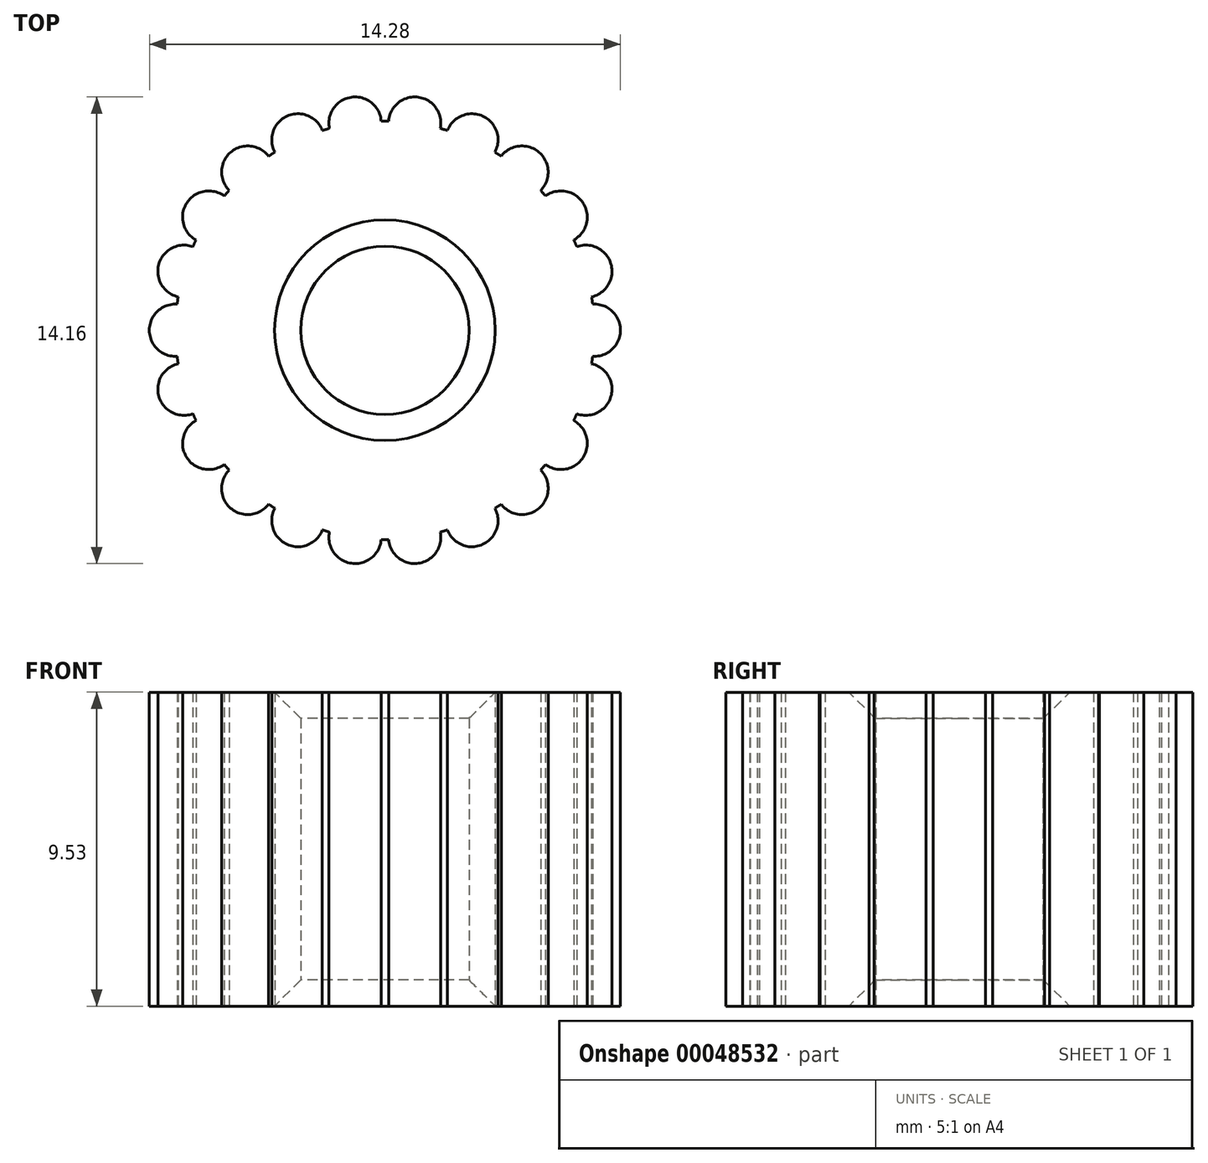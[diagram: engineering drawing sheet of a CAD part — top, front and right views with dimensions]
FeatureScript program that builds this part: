
annotation { "Feature Type Name" : "Feature", "Feature Type Description" : "" }
export const myFeature = defineFeature(function(context is Context, id is Id, definition is map)
    precondition{}
    {
        {
            var Q0;
            Q0=qCreatedBy(makeId("Top.planeOp"),FACE);
            var sketch = newSketch(context, id + "F0", { "sketchPlane" : qUnion([Q0])});
            skCircle(sketch, "E0", {"center": v(0, 0) * mm, "radius": 2.55 * mm});
            skCircle(sketch, "E1", {"center": v(0, 0) * mm, "radius": 6.35 * mm});
            skCircle(sketch, "E2", {"center": v(-6.35, 0) * mm, "radius": 0.8 * mm});
            skCircle(sketch, "E3.1.0", {"center": v(-6.1, -1.79) * mm, "radius": 0.8 * mm});
            skCircle(sketch, "E3.2.0", {"center": v(-5.34, -3.43) * mm, "radius": 0.8 * mm});
            skCircle(sketch, "E3.3.0", {"center": v(-4.16, -4.8) * mm, "radius": 0.8 * mm});
            skCircle(sketch, "E3.4.0", {"center": v(-2.64, -5.78) * mm, "radius": 0.8 * mm});
            skCircle(sketch, "E3.5.0", {"center": v(-0.9, -6.29) * mm, "radius": 0.8 * mm});
            skCircle(sketch, "E3.6.0", {"center": v(0.9, -6.29) * mm, "radius": 0.8 * mm});
            skCircle(sketch, "E3.7.0", {"center": v(2.64, -5.78) * mm, "radius": 0.8 * mm});
            skCircle(sketch, "E3.8.0", {"center": v(4.16, -4.8) * mm, "radius": 0.8 * mm});
            skCircle(sketch, "E3.9.0", {"center": v(5.34, -3.43) * mm, "radius": 0.8 * mm});
            skCircle(sketch, "E3.10.0", {"center": v(6.1, -1.79) * mm, "radius": 0.8 * mm});
            skCircle(sketch, "E3.11.0", {"center": v(6.35, 0) * mm, "radius": 0.8 * mm});
            skCircle(sketch, "E3.12.0", {"center": v(6.1, 1.79) * mm, "radius": 0.8 * mm});
            skCircle(sketch, "E3.13.0", {"center": v(5.34, 3.43) * mm, "radius": 0.8 * mm});
            skCircle(sketch, "E3.14.0", {"center": v(4.16, 4.8) * mm, "radius": 0.8 * mm});
            skCircle(sketch, "E3.15.0", {"center": v(2.64, 5.78) * mm, "radius": 0.8 * mm});
            skCircle(sketch, "E3.16.0", {"center": v(0.9, 6.29) * mm, "radius": 0.8 * mm});
            skCircle(sketch, "E3.17.0", {"center": v(-0.9, 6.29) * mm, "radius": 0.8 * mm});
            skCircle(sketch, "E3.18.0", {"center": v(-2.64, 5.78) * mm, "radius": 0.8 * mm});
            skCircle(sketch, "E3.19.0", {"center": v(-4.16, 4.8) * mm, "radius": 0.8 * mm});
            skCircle(sketch, "E3.20.0", {"center": v(-5.34, 3.43) * mm, "radius": 0.8 * mm});
            skCircle(sketch, "E3.21.0", {"center": v(-6.1, 1.79) * mm, "radius": 0.8 * mm});
            skSolve(sketch);
        }
        {
            var Q0;
            Q0=makeQuery(id+"F0.imprint","IMPRINT",FACE,{"disambiguationData":[TD([[makeQuery(id+"F0.imprint","IMPRINT",EDGE,{"derivedFrom":sQuery(id+"F0.wireOp",EDGE,"E0")}),-1.0]])]});
            var Q1;
            {var subQ0=sQuery(id+"F0.wireOp",EDGE,"E3.19.0");var subQ1=sQuery(id+"F0.wireOp",EDGE,"E1");var subQ3=makeQuery(id+"F0.imprint","INTERSECT",VERTEX,{"disambiguationData":[OD(0.0)],"derivedFrom":[subQ1,subQ0]});Q1=makeQuery(id+"F0.imprint","IMPRINT",FACE,{"disambiguationData":[TD([[makeQuery(id+"F0.imprint","IMPRINT",EDGE,{"disambiguationData":[TD([[subQ3,-1.0]])],"derivedFrom":subQ1}),1.0]])]});}
            var Q2;
            {var subQ0=sQuery(id+"F0.wireOp",EDGE,"E3.18.0");var subQ1=sQuery(id+"F0.wireOp",EDGE,"E1");var subQ3=makeQuery(id+"F0.imprint","INTERSECT",VERTEX,{"disambiguationData":[OD(0.0)],"derivedFrom":[subQ1,subQ0]});Q2=makeQuery(id+"F0.imprint","IMPRINT",FACE,{"disambiguationData":[TD([[makeQuery(id+"F0.imprint","IMPRINT",EDGE,{"disambiguationData":[TD([[subQ3,-1.0]])],"derivedFrom":subQ1}),1.0]])]});}
            var Q3;
            {var subQ0=sQuery(id+"F0.wireOp",EDGE,"E3.17.0");var subQ1=sQuery(id+"F0.wireOp",EDGE,"E1");var subQ3=makeQuery(id+"F0.imprint","INTERSECT",VERTEX,{"disambiguationData":[OD(0.0)],"derivedFrom":[subQ1,subQ0]});Q3=makeQuery(id+"F0.imprint","IMPRINT",FACE,{"disambiguationData":[TD([[makeQuery(id+"F0.imprint","IMPRINT",EDGE,{"disambiguationData":[TD([[subQ3,-1.0]])],"derivedFrom":subQ1}),1.0]])]});}
            var Q4;
            {var subQ0=sQuery(id+"F0.wireOp",EDGE,"E3.16.0");var subQ1=sQuery(id+"F0.wireOp",EDGE,"E1");var subQ3=makeQuery(id+"F0.imprint","INTERSECT",VERTEX,{"disambiguationData":[OD(0.0)],"derivedFrom":[subQ1,subQ0]});Q4=makeQuery(id+"F0.imprint","IMPRINT",FACE,{"disambiguationData":[TD([[makeQuery(id+"F0.imprint","IMPRINT",EDGE,{"disambiguationData":[TD([[subQ3,-1.0]])],"derivedFrom":subQ1}),1.0]])]});}
            var Q5;
            {var subQ0=sQuery(id+"F0.wireOp",EDGE,"E3.15.0");var subQ1=sQuery(id+"F0.wireOp",EDGE,"E1");var subQ3=makeQuery(id+"F0.imprint","INTERSECT",VERTEX,{"disambiguationData":[OD(0.0)],"derivedFrom":[subQ1,subQ0]});Q5=makeQuery(id+"F0.imprint","IMPRINT",FACE,{"disambiguationData":[TD([[makeQuery(id+"F0.imprint","IMPRINT",EDGE,{"disambiguationData":[TD([[subQ3,-1.0]])],"derivedFrom":subQ1}),1.0]])]});}
            var Q6;
            {var subQ0=sQuery(id+"F0.wireOp",EDGE,"E3.14.0");var subQ1=sQuery(id+"F0.wireOp",EDGE,"E1");var subQ3=makeQuery(id+"F0.imprint","INTERSECT",VERTEX,{"disambiguationData":[OD(0.0)],"derivedFrom":[subQ1,subQ0]});Q6=makeQuery(id+"F0.imprint","IMPRINT",FACE,{"disambiguationData":[TD([[makeQuery(id+"F0.imprint","IMPRINT",EDGE,{"disambiguationData":[TD([[subQ3,-1.0]])],"derivedFrom":subQ1}),1.0]])]});}
            var Q7;
            {var subQ0=sQuery(id+"F0.wireOp",EDGE,"E3.13.0");var subQ1=sQuery(id+"F0.wireOp",EDGE,"E1");var subQ3=makeQuery(id+"F0.imprint","INTERSECT",VERTEX,{"disambiguationData":[OD(0.0)],"derivedFrom":[subQ1,subQ0]});Q7=makeQuery(id+"F0.imprint","IMPRINT",FACE,{"disambiguationData":[TD([[makeQuery(id+"F0.imprint","IMPRINT",EDGE,{"disambiguationData":[TD([[subQ3,-1.0]])],"derivedFrom":subQ1}),1.0]])]});}
            var Q8;
            {var subQ0=sQuery(id+"F0.wireOp",EDGE,"E3.12.0");var subQ1=sQuery(id+"F0.wireOp",EDGE,"E1");var subQ3=makeQuery(id+"F0.imprint","INTERSECT",VERTEX,{"disambiguationData":[OD(0.0)],"derivedFrom":[subQ1,subQ0]});Q8=makeQuery(id+"F0.imprint","IMPRINT",FACE,{"disambiguationData":[TD([[makeQuery(id+"F0.imprint","IMPRINT",EDGE,{"disambiguationData":[TD([[subQ3,-1.0]])],"derivedFrom":subQ1}),1.0]])]});}
            var Q9;
            {var subQ0=sQuery(id+"F0.wireOp",EDGE,"E3.11.0");var subQ1=sQuery(id+"F0.wireOp",EDGE,"E1");var subQ3=makeQuery(id+"F0.imprint","INTERSECT",VERTEX,{"disambiguationData":[OD(0.0)],"derivedFrom":[subQ1,subQ0]});Q9=makeQuery(id+"F0.imprint","IMPRINT",FACE,{"disambiguationData":[TD([[makeQuery(id+"F0.imprint","IMPRINT",EDGE,{"disambiguationData":[TD([[subQ3,1.0]])],"derivedFrom":subQ1}),1.0]])]});}
            var Q10;
            {var subQ0=sQuery(id+"F0.wireOp",EDGE,"E3.10.0");var subQ1=sQuery(id+"F0.wireOp",EDGE,"E1");var subQ3=makeQuery(id+"F0.imprint","INTERSECT",VERTEX,{"disambiguationData":[OD(0.0)],"derivedFrom":[subQ1,subQ0]});Q10=makeQuery(id+"F0.imprint","IMPRINT",FACE,{"disambiguationData":[TD([[makeQuery(id+"F0.imprint","IMPRINT",EDGE,{"disambiguationData":[TD([[subQ3,-1.0]])],"derivedFrom":subQ1}),1.0]])]});}
            var Q11;
            {var subQ0=sQuery(id+"F0.wireOp",EDGE,"E3.9.0");var subQ1=sQuery(id+"F0.wireOp",EDGE,"E1");var subQ3=makeQuery(id+"F0.imprint","INTERSECT",VERTEX,{"disambiguationData":[OD(0.0)],"derivedFrom":[subQ1,subQ0]});Q11=makeQuery(id+"F0.imprint","IMPRINT",FACE,{"disambiguationData":[TD([[makeQuery(id+"F0.imprint","IMPRINT",EDGE,{"disambiguationData":[TD([[subQ3,-1.0]])],"derivedFrom":subQ1}),1.0]])]});}
            var Q12;
            {var subQ0=sQuery(id+"F0.wireOp",EDGE,"E3.8.0");var subQ1=sQuery(id+"F0.wireOp",EDGE,"E1");var subQ3=makeQuery(id+"F0.imprint","INTERSECT",VERTEX,{"disambiguationData":[OD(0.0)],"derivedFrom":[subQ1,subQ0]});Q12=makeQuery(id+"F0.imprint","IMPRINT",FACE,{"disambiguationData":[TD([[makeQuery(id+"F0.imprint","IMPRINT",EDGE,{"disambiguationData":[TD([[subQ3,-1.0]])],"derivedFrom":subQ1}),1.0]])]});}
            var Q13;
            {var subQ0=sQuery(id+"F0.wireOp",EDGE,"E3.7.0");var subQ1=sQuery(id+"F0.wireOp",EDGE,"E1");var subQ3=makeQuery(id+"F0.imprint","INTERSECT",VERTEX,{"disambiguationData":[OD(0.0)],"derivedFrom":[subQ1,subQ0]});Q13=makeQuery(id+"F0.imprint","IMPRINT",FACE,{"disambiguationData":[TD([[makeQuery(id+"F0.imprint","IMPRINT",EDGE,{"disambiguationData":[TD([[subQ3,-1.0]])],"derivedFrom":subQ1}),1.0]])]});}
            var Q14;
            {var subQ0=sQuery(id+"F0.wireOp",EDGE,"E3.6.0");var subQ1=sQuery(id+"F0.wireOp",EDGE,"E1");var subQ3=makeQuery(id+"F0.imprint","INTERSECT",VERTEX,{"disambiguationData":[OD(0.0)],"derivedFrom":[subQ1,subQ0]});Q14=makeQuery(id+"F0.imprint","IMPRINT",FACE,{"disambiguationData":[TD([[makeQuery(id+"F0.imprint","IMPRINT",EDGE,{"disambiguationData":[TD([[subQ3,-1.0]])],"derivedFrom":subQ1}),1.0]])]});}
            var Q15;
            {var subQ0=sQuery(id+"F0.wireOp",EDGE,"E3.5.0");var subQ1=sQuery(id+"F0.wireOp",EDGE,"E1");var subQ3=makeQuery(id+"F0.imprint","INTERSECT",VERTEX,{"disambiguationData":[OD(0.0)],"derivedFrom":[subQ1,subQ0]});Q15=makeQuery(id+"F0.imprint","IMPRINT",FACE,{"disambiguationData":[TD([[makeQuery(id+"F0.imprint","IMPRINT",EDGE,{"disambiguationData":[TD([[subQ3,-1.0]])],"derivedFrom":subQ1}),1.0]])]});}
            var Q16;
            {var subQ0=sQuery(id+"F0.wireOp",EDGE,"E3.4.0");var subQ1=sQuery(id+"F0.wireOp",EDGE,"E1");var subQ3=makeQuery(id+"F0.imprint","INTERSECT",VERTEX,{"disambiguationData":[OD(0.0)],"derivedFrom":[subQ1,subQ0]});Q16=makeQuery(id+"F0.imprint","IMPRINT",FACE,{"disambiguationData":[TD([[makeQuery(id+"F0.imprint","IMPRINT",EDGE,{"disambiguationData":[TD([[subQ3,-1.0]])],"derivedFrom":subQ1}),1.0]])]});}
            var Q17;
            {var subQ0=sQuery(id+"F0.wireOp",EDGE,"E3.3.0");var subQ1=sQuery(id+"F0.wireOp",EDGE,"E1");var subQ3=makeQuery(id+"F0.imprint","INTERSECT",VERTEX,{"disambiguationData":[OD(0.0)],"derivedFrom":[subQ1,subQ0]});Q17=makeQuery(id+"F0.imprint","IMPRINT",FACE,{"disambiguationData":[TD([[makeQuery(id+"F0.imprint","IMPRINT",EDGE,{"disambiguationData":[TD([[subQ3,-1.0]])],"derivedFrom":subQ1}),1.0]])]});}
            var Q18;
            {var subQ0=sQuery(id+"F0.wireOp",EDGE,"E3.2.0");var subQ1=sQuery(id+"F0.wireOp",EDGE,"E1");var subQ3=makeQuery(id+"F0.imprint","INTERSECT",VERTEX,{"disambiguationData":[OD(0.0)],"derivedFrom":[subQ1,subQ0]});Q18=makeQuery(id+"F0.imprint","IMPRINT",FACE,{"disambiguationData":[TD([[makeQuery(id+"F0.imprint","IMPRINT",EDGE,{"disambiguationData":[TD([[subQ3,-1.0]])],"derivedFrom":subQ1}),1.0]])]});}
            var Q19;
            {var subQ0=sQuery(id+"F0.wireOp",EDGE,"E3.1.0");var subQ1=sQuery(id+"F0.wireOp",EDGE,"E1");var subQ3=makeQuery(id+"F0.imprint","INTERSECT",VERTEX,{"disambiguationData":[OD(0.0)],"derivedFrom":[subQ1,subQ0]});Q19=makeQuery(id+"F0.imprint","IMPRINT",FACE,{"disambiguationData":[TD([[makeQuery(id+"F0.imprint","IMPRINT",EDGE,{"disambiguationData":[TD([[subQ3,-1.0]])],"derivedFrom":subQ1}),1.0]])]});}
            var Q20;
            {var subQ0=sQuery(id+"F0.wireOp",EDGE,"E2");var subQ1=sQuery(id+"F0.wireOp",EDGE,"E1");var subQ3=makeQuery(id+"F0.imprint","INTERSECT",VERTEX,{"disambiguationData":[OD(0.0)],"derivedFrom":[subQ1,subQ0]});Q20=makeQuery(id+"F0.imprint","IMPRINT",FACE,{"disambiguationData":[TD([[makeQuery(id+"F0.imprint","IMPRINT",EDGE,{"disambiguationData":[TD([[subQ3,-1.0]])],"derivedFrom":subQ1}),1.0]])]});}
            var Q21;
            {var subQ0=sQuery(id+"F0.wireOp",EDGE,"E3.21.0");var subQ1=sQuery(id+"F0.wireOp",EDGE,"E1");var subQ3=makeQuery(id+"F0.imprint","INTERSECT",VERTEX,{"disambiguationData":[OD(0.0)],"derivedFrom":[subQ1,subQ0]});Q21=makeQuery(id+"F0.imprint","IMPRINT",FACE,{"disambiguationData":[TD([[makeQuery(id+"F0.imprint","IMPRINT",EDGE,{"disambiguationData":[TD([[subQ3,-1.0]])],"derivedFrom":subQ1}),1.0]])]});}
            var Q22;
            {var subQ0=sQuery(id+"F0.wireOp",EDGE,"E3.20.0");var subQ1=sQuery(id+"F0.wireOp",EDGE,"E1");var subQ3=makeQuery(id+"F0.imprint","INTERSECT",VERTEX,{"disambiguationData":[OD(0.0)],"derivedFrom":[subQ1,subQ0]});Q22=makeQuery(id+"F0.imprint","IMPRINT",FACE,{"disambiguationData":[TD([[makeQuery(id+"F0.imprint","IMPRINT",EDGE,{"disambiguationData":[TD([[subQ3,-1.0]])],"derivedFrom":subQ1}),1.0]])]});}
            var Q23;
            {var subQ0=sQuery(id+"F0.wireOp",EDGE,"E3.17.0");var subQ1=sQuery(id+"F0.wireOp",EDGE,"E1");var subQ3=makeQuery(id+"F0.imprint","INTERSECT",VERTEX,{"disambiguationData":[OD(0.0)],"derivedFrom":[subQ1,subQ0]});Q23=makeQuery(id+"F0.imprint","IMPRINT",FACE,{"disambiguationData":[TD([[makeQuery(id+"F0.imprint","IMPRINT",EDGE,{"disambiguationData":[TD([[subQ3,-1.0]])],"derivedFrom":subQ1}),-1.0]])]});}
            var Q24;
            {var subQ0=sQuery(id+"F0.wireOp",EDGE,"E3.16.0");var subQ1=sQuery(id+"F0.wireOp",EDGE,"E1");var subQ3=makeQuery(id+"F0.imprint","INTERSECT",VERTEX,{"disambiguationData":[OD(0.0)],"derivedFrom":[subQ1,subQ0]});Q24=makeQuery(id+"F0.imprint","IMPRINT",FACE,{"disambiguationData":[TD([[makeQuery(id+"F0.imprint","IMPRINT",EDGE,{"disambiguationData":[TD([[subQ3,-1.0]])],"derivedFrom":subQ1}),-1.0]])]});}
            var Q25;
            {var subQ0=sQuery(id+"F0.wireOp",EDGE,"E3.15.0");var subQ1=sQuery(id+"F0.wireOp",EDGE,"E1");var subQ3=makeQuery(id+"F0.imprint","INTERSECT",VERTEX,{"disambiguationData":[OD(0.0)],"derivedFrom":[subQ1,subQ0]});Q25=makeQuery(id+"F0.imprint","IMPRINT",FACE,{"disambiguationData":[TD([[makeQuery(id+"F0.imprint","IMPRINT",EDGE,{"disambiguationData":[TD([[subQ3,-1.0]])],"derivedFrom":subQ1}),-1.0]])]});}
            var Q26;
            {var subQ0=sQuery(id+"F0.wireOp",EDGE,"E3.14.0");var subQ1=sQuery(id+"F0.wireOp",EDGE,"E1");var subQ3=makeQuery(id+"F0.imprint","INTERSECT",VERTEX,{"disambiguationData":[OD(0.0)],"derivedFrom":[subQ1,subQ0]});Q26=makeQuery(id+"F0.imprint","IMPRINT",FACE,{"disambiguationData":[TD([[makeQuery(id+"F0.imprint","IMPRINT",EDGE,{"disambiguationData":[TD([[subQ3,-1.0]])],"derivedFrom":subQ1}),-1.0]])]});}
            var Q27;
            {var subQ0=sQuery(id+"F0.wireOp",EDGE,"E3.13.0");var subQ1=sQuery(id+"F0.wireOp",EDGE,"E1");var subQ3=makeQuery(id+"F0.imprint","INTERSECT",VERTEX,{"disambiguationData":[OD(0.0)],"derivedFrom":[subQ1,subQ0]});Q27=makeQuery(id+"F0.imprint","IMPRINT",FACE,{"disambiguationData":[TD([[makeQuery(id+"F0.imprint","IMPRINT",EDGE,{"disambiguationData":[TD([[subQ3,-1.0]])],"derivedFrom":subQ1}),-1.0]])]});}
            var Q28;
            {var subQ0=sQuery(id+"F0.wireOp",EDGE,"E3.12.0");var subQ1=sQuery(id+"F0.wireOp",EDGE,"E1");var subQ3=makeQuery(id+"F0.imprint","INTERSECT",VERTEX,{"disambiguationData":[OD(0.0)],"derivedFrom":[subQ1,subQ0]});Q28=makeQuery(id+"F0.imprint","IMPRINT",FACE,{"disambiguationData":[TD([[makeQuery(id+"F0.imprint","IMPRINT",EDGE,{"disambiguationData":[TD([[subQ3,-1.0]])],"derivedFrom":subQ1}),-1.0]])]});}
            var Q29;
            {var subQ0=sQuery(id+"F0.wireOp",EDGE,"E3.11.0");var subQ1=sQuery(id+"F0.wireOp",EDGE,"E1");var subQ3=makeQuery(id+"F0.imprint","INTERSECT",VERTEX,{"disambiguationData":[OD(0.0)],"derivedFrom":[subQ1,subQ0]});Q29=makeQuery(id+"F0.imprint","IMPRINT",FACE,{"disambiguationData":[TD([[makeQuery(id+"F0.imprint","IMPRINT",EDGE,{"disambiguationData":[TD([[subQ3,1.0]])],"derivedFrom":subQ1}),-1.0]])]});}
            var Q30;
            {var subQ0=sQuery(id+"F0.wireOp",EDGE,"E3.10.0");var subQ1=sQuery(id+"F0.wireOp",EDGE,"E1");var subQ3=makeQuery(id+"F0.imprint","INTERSECT",VERTEX,{"disambiguationData":[OD(0.0)],"derivedFrom":[subQ1,subQ0]});Q30=makeQuery(id+"F0.imprint","IMPRINT",FACE,{"disambiguationData":[TD([[makeQuery(id+"F0.imprint","IMPRINT",EDGE,{"disambiguationData":[TD([[subQ3,-1.0]])],"derivedFrom":subQ1}),-1.0]])]});}
            var Q31;
            {var subQ0=sQuery(id+"F0.wireOp",EDGE,"E3.9.0");var subQ1=sQuery(id+"F0.wireOp",EDGE,"E1");var subQ3=makeQuery(id+"F0.imprint","INTERSECT",VERTEX,{"disambiguationData":[OD(0.0)],"derivedFrom":[subQ1,subQ0]});Q31=makeQuery(id+"F0.imprint","IMPRINT",FACE,{"disambiguationData":[TD([[makeQuery(id+"F0.imprint","IMPRINT",EDGE,{"disambiguationData":[TD([[subQ3,-1.0]])],"derivedFrom":subQ1}),-1.0]])]});}
            var Q32;
            {var subQ0=sQuery(id+"F0.wireOp",EDGE,"E3.8.0");var subQ1=sQuery(id+"F0.wireOp",EDGE,"E1");var subQ3=makeQuery(id+"F0.imprint","INTERSECT",VERTEX,{"disambiguationData":[OD(0.0)],"derivedFrom":[subQ1,subQ0]});Q32=makeQuery(id+"F0.imprint","IMPRINT",FACE,{"disambiguationData":[TD([[makeQuery(id+"F0.imprint","IMPRINT",EDGE,{"disambiguationData":[TD([[subQ3,-1.0]])],"derivedFrom":subQ1}),-1.0]])]});}
            var Q33;
            {var subQ0=sQuery(id+"F0.wireOp",EDGE,"E3.7.0");var subQ1=sQuery(id+"F0.wireOp",EDGE,"E1");var subQ3=makeQuery(id+"F0.imprint","INTERSECT",VERTEX,{"disambiguationData":[OD(0.0)],"derivedFrom":[subQ1,subQ0]});Q33=makeQuery(id+"F0.imprint","IMPRINT",FACE,{"disambiguationData":[TD([[makeQuery(id+"F0.imprint","IMPRINT",EDGE,{"disambiguationData":[TD([[subQ3,-1.0]])],"derivedFrom":subQ1}),-1.0]])]});}
            var Q34;
            {var subQ0=sQuery(id+"F0.wireOp",EDGE,"E3.6.0");var subQ1=sQuery(id+"F0.wireOp",EDGE,"E1");var subQ3=makeQuery(id+"F0.imprint","INTERSECT",VERTEX,{"disambiguationData":[OD(0.0)],"derivedFrom":[subQ1,subQ0]});Q34=makeQuery(id+"F0.imprint","IMPRINT",FACE,{"disambiguationData":[TD([[makeQuery(id+"F0.imprint","IMPRINT",EDGE,{"disambiguationData":[TD([[subQ3,-1.0]])],"derivedFrom":subQ1}),-1.0]])]});}
            var Q35;
            {var subQ0=sQuery(id+"F0.wireOp",EDGE,"E3.5.0");var subQ1=sQuery(id+"F0.wireOp",EDGE,"E1");var subQ3=makeQuery(id+"F0.imprint","INTERSECT",VERTEX,{"disambiguationData":[OD(0.0)],"derivedFrom":[subQ1,subQ0]});Q35=makeQuery(id+"F0.imprint","IMPRINT",FACE,{"disambiguationData":[TD([[makeQuery(id+"F0.imprint","IMPRINT",EDGE,{"disambiguationData":[TD([[subQ3,-1.0]])],"derivedFrom":subQ1}),-1.0]])]});}
            var Q36;
            {var subQ0=sQuery(id+"F0.wireOp",EDGE,"E3.4.0");var subQ1=sQuery(id+"F0.wireOp",EDGE,"E1");var subQ3=makeQuery(id+"F0.imprint","INTERSECT",VERTEX,{"disambiguationData":[OD(0.0)],"derivedFrom":[subQ1,subQ0]});Q36=makeQuery(id+"F0.imprint","IMPRINT",FACE,{"disambiguationData":[TD([[makeQuery(id+"F0.imprint","IMPRINT",EDGE,{"disambiguationData":[TD([[subQ3,-1.0]])],"derivedFrom":subQ1}),-1.0]])]});}
            var Q37;
            {var subQ0=sQuery(id+"F0.wireOp",EDGE,"E3.3.0");var subQ1=sQuery(id+"F0.wireOp",EDGE,"E1");var subQ3=makeQuery(id+"F0.imprint","INTERSECT",VERTEX,{"disambiguationData":[OD(0.0)],"derivedFrom":[subQ1,subQ0]});Q37=makeQuery(id+"F0.imprint","IMPRINT",FACE,{"disambiguationData":[TD([[makeQuery(id+"F0.imprint","IMPRINT",EDGE,{"disambiguationData":[TD([[subQ3,-1.0]])],"derivedFrom":subQ1}),-1.0]])]});}
            var Q38;
            {var subQ0=sQuery(id+"F0.wireOp",EDGE,"E3.2.0");var subQ1=sQuery(id+"F0.wireOp",EDGE,"E1");var subQ3=makeQuery(id+"F0.imprint","INTERSECT",VERTEX,{"disambiguationData":[OD(0.0)],"derivedFrom":[subQ1,subQ0]});Q38=makeQuery(id+"F0.imprint","IMPRINT",FACE,{"disambiguationData":[TD([[makeQuery(id+"F0.imprint","IMPRINT",EDGE,{"disambiguationData":[TD([[subQ3,-1.0]])],"derivedFrom":subQ1}),-1.0]])]});}
            var Q39;
            {var subQ0=sQuery(id+"F0.wireOp",EDGE,"E3.1.0");var subQ1=sQuery(id+"F0.wireOp",EDGE,"E1");var subQ3=makeQuery(id+"F0.imprint","INTERSECT",VERTEX,{"disambiguationData":[OD(0.0)],"derivedFrom":[subQ1,subQ0]});Q39=makeQuery(id+"F0.imprint","IMPRINT",FACE,{"disambiguationData":[TD([[makeQuery(id+"F0.imprint","IMPRINT",EDGE,{"disambiguationData":[TD([[subQ3,-1.0]])],"derivedFrom":subQ1}),-1.0]])]});}
            var Q40;
            {var subQ0=sQuery(id+"F0.wireOp",EDGE,"E2");var subQ1=sQuery(id+"F0.wireOp",EDGE,"E1");var subQ3=makeQuery(id+"F0.imprint","INTERSECT",VERTEX,{"disambiguationData":[OD(0.0)],"derivedFrom":[subQ1,subQ0]});Q40=makeQuery(id+"F0.imprint","IMPRINT",FACE,{"disambiguationData":[TD([[makeQuery(id+"F0.imprint","IMPRINT",EDGE,{"disambiguationData":[TD([[subQ3,-1.0]])],"derivedFrom":subQ1}),-1.0]])]});}
            var Q41;
            {var subQ0=sQuery(id+"F0.wireOp",EDGE,"E3.21.0");var subQ1=sQuery(id+"F0.wireOp",EDGE,"E1");var subQ3=makeQuery(id+"F0.imprint","INTERSECT",VERTEX,{"disambiguationData":[OD(0.0)],"derivedFrom":[subQ1,subQ0]});Q41=makeQuery(id+"F0.imprint","IMPRINT",FACE,{"disambiguationData":[TD([[makeQuery(id+"F0.imprint","IMPRINT",EDGE,{"disambiguationData":[TD([[subQ3,-1.0]])],"derivedFrom":subQ1}),-1.0]])]});}
            var Q42;
            {var subQ0=sQuery(id+"F0.wireOp",EDGE,"E3.20.0");var subQ1=sQuery(id+"F0.wireOp",EDGE,"E1");var subQ3=makeQuery(id+"F0.imprint","INTERSECT",VERTEX,{"disambiguationData":[OD(0.0)],"derivedFrom":[subQ1,subQ0]});Q42=makeQuery(id+"F0.imprint","IMPRINT",FACE,{"disambiguationData":[TD([[makeQuery(id+"F0.imprint","IMPRINT",EDGE,{"disambiguationData":[TD([[subQ3,-1.0]])],"derivedFrom":subQ1}),-1.0]])]});}
            var Q43;
            {var subQ0=sQuery(id+"F0.wireOp",EDGE,"E3.19.0");var subQ1=sQuery(id+"F0.wireOp",EDGE,"E1");var subQ3=makeQuery(id+"F0.imprint","INTERSECT",VERTEX,{"disambiguationData":[OD(0.0)],"derivedFrom":[subQ1,subQ0]});Q43=makeQuery(id+"F0.imprint","IMPRINT",FACE,{"disambiguationData":[TD([[makeQuery(id+"F0.imprint","IMPRINT",EDGE,{"disambiguationData":[TD([[subQ3,-1.0]])],"derivedFrom":subQ1}),-1.0]])]});}
            var Q44;
            {var subQ0=sQuery(id+"F0.wireOp",EDGE,"E3.18.0");var subQ1=sQuery(id+"F0.wireOp",EDGE,"E1");var subQ3=makeQuery(id+"F0.imprint","INTERSECT",VERTEX,{"disambiguationData":[OD(0.0)],"derivedFrom":[subQ1,subQ0]});Q44=makeQuery(id+"F0.imprint","IMPRINT",FACE,{"disambiguationData":[TD([[makeQuery(id+"F0.imprint","IMPRINT",EDGE,{"disambiguationData":[TD([[subQ3,-1.0]])],"derivedFrom":subQ1}),-1.0]])]});}
            extrude(context, id + "F1", {"entities" : qUnion([Q0, Q1, Q2, Q3, Q4, Q5, Q6, Q7, Q8, Q9, Q10, Q11, Q12, Q13, Q14, Q15, Q16, Q17, Q18, Q19, Q20, Q21, Q22, Q23, Q24, Q25, Q26, Q27, Q28, Q29, Q30, Q31, Q32, Q33, Q34, Q35, Q36, Q37, Q38, Q39, Q40, Q41, Q42, Q43, Q44]), "depth" : 9.52 * mm});
        }
        {
            var Q0;
            Q0=makeQuery(id+"F1.opExtrude","SWEPT_FACE",FACE,{"disambiguationData":[OSD([sQuery(id+"F0.wireOp",EDGE,"E0")])]});
            chamfer(context, id + "F2", {"entities" : qUnion([Q0]), "width" : 0.8 * mm, "tangentPropagation" : true});
        }
    });
